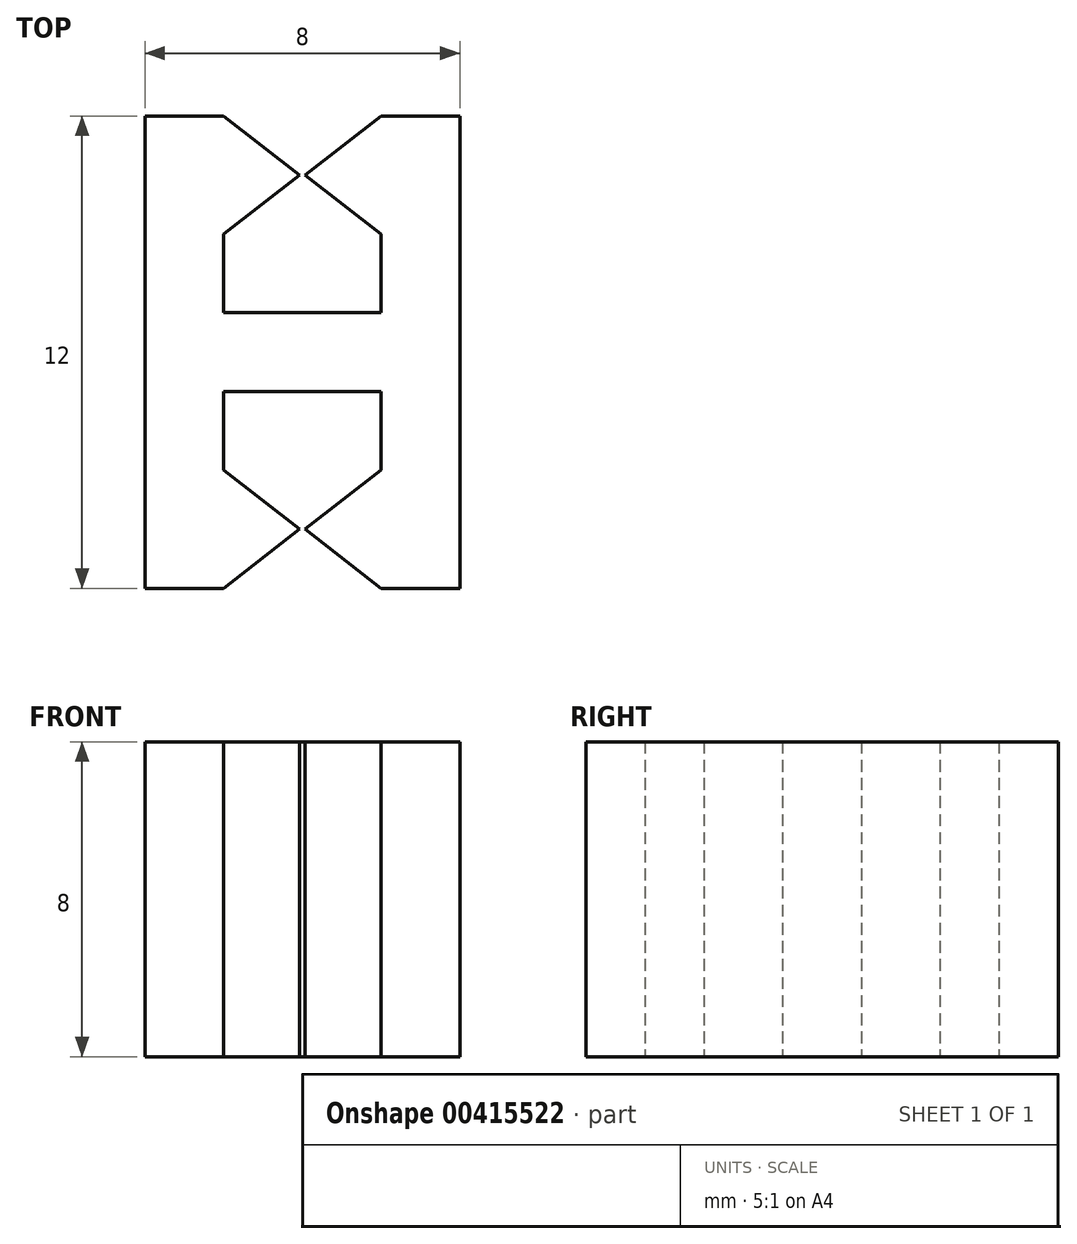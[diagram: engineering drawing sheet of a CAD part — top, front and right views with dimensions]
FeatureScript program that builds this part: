
annotation { "Feature Type Name" : "Feature", "Feature Type Description" : "" }
export const myFeature = defineFeature(function(context is Context, id is Id, definition is map)
    precondition{}
    {
        {
            var Q0;
            Q0=qCreatedBy(makeId("Top.planeOp"),FACE);
            var sketch = newSketch(context, id + "F0", { "sketchPlane" : qUnion([Q0])});
            skLineSegment(sketch, "E0", {"start": v(0, -1.2) * mm, "end": v(-2, -1.2) * mm});
            skLineSegment(sketch, "E1", {"start": v(-2, -1.2) * mm, "end": v(-2, -2.62) * mm});
            skLineSegment(sketch, "E2", {"start": v(-1.95, -2.76) * mm, "end": v(-1.4, -3.38) * mm});
            skLineSegment(sketch, "E3", {"start": v(-1.35, -3.45) * mm, "end": v(-1.35, -6) * mm, "construction": true});
            skLineSegment(sketch, "E4", {"start": v(-1.35, -6) * mm, "end": v(-4, -6) * mm});
            skLineSegment(sketch, "E5", {"start": v(-4, -6) * mm, "end": v(-4, 0) * mm});
            skArc(sketch, "E6", {"start": v(-1.35, -6) * mm, "mid": v(-0.07, -4.77) * mm, "end": v(-1.26, -3.45) * mm});
            skPoint(sketch, "E7.visualSharp", {"position": v(-2, -2.7) * mm});
            skArc(sketch, "E7.filletArc", {"start": v(-2, -2.62) * mm, "mid": v(-1.99, -2.7) * mm, "end": v(-1.95, -2.76) * mm});
            skPoint(sketch, "E8.visualSharp", {"position": v(-1.35, -3.45) * mm});
            skArc(sketch, "E8.filletArc", {"start": v(-1.4, -3.38) * mm, "mid": v(-1.34, -3.43) * mm, "end": v(-1.26, -3.45) * mm});
            skLineSegment(sketch, "E9", {"start": v(0, 0) * mm, "end": v(0, -3.87) * mm, "construction": true});
            skLineSegment(sketch, "E10", {"start": v(0, 0) * mm, "end": v(-4.58, 0) * mm, "construction": true});
            skArc(sketch, "E11.MirrorCS", {"start": v(1.4, -3.38) * mm, "mid": v(1.34, -3.43) * mm, "end": v(1.26, -3.45) * mm});
            skArc(sketch, "E12.MirrorCS", {"start": v(2, -2.62) * mm, "mid": v(1.99, -2.7) * mm, "end": v(1.95, -2.76) * mm});
            skPoint(sketch, "E13.MirrorP", {"position": v(1.35, -3.45) * mm});
            skPoint(sketch, "E14.MirrorP", {"position": v(2, -2.7) * mm});
            skArc(sketch, "E15.MirrorCS", {"start": v(1.35, -6) * mm, "mid": v(0.07, -4.77) * mm, "end": v(1.26, -3.45) * mm});
            skLineSegment(sketch, "E16.MirrorCS", {"start": v(0, -1.2) * mm, "end": v(2, -1.2) * mm});
            skLineSegment(sketch, "E17.MirrorCS", {"start": v(2, -1.2) * mm, "end": v(2, -2.62) * mm});
            skLineSegment(sketch, "E18.MirrorCS", {"start": v(1.35, -3.45) * mm, "end": v(1.35, -6) * mm, "construction": true});
            skLineSegment(sketch, "E19.MirrorCS", {"start": v(1.95, -2.76) * mm, "end": v(1.4, -3.38) * mm});
            skLineSegment(sketch, "E20.MirrorCS", {"start": v(1.35, -6) * mm, "end": v(4, -6) * mm});
            skLineSegment(sketch, "E21.MirrorCS", {"start": v(4, -6) * mm, "end": v(4, 0) * mm});
            skArc(sketch, "E22.MirrorCS", {"start": v(-1.4, 3.38) * mm, "mid": v(-1.34, 3.43) * mm, "end": v(-1.26, 3.45) * mm});
            skArc(sketch, "E23.MirrorCS", {"start": v(1.4, 3.38) * mm, "mid": v(1.34, 3.43) * mm, "end": v(1.26, 3.45) * mm});
            skLineSegment(sketch, "E24.MirrorCS", {"start": v(0, 1.2) * mm, "end": v(-2, 1.2) * mm});
            skLineSegment(sketch, "E25.MirrorCS", {"start": v(2, 1.2) * mm, "end": v(2, 2.62) * mm});
            skPoint(sketch, "E26.MirrorP", {"position": v(1.35, 3.45) * mm});
            skLineSegment(sketch, "E27.MirrorCS", {"start": v(0, 1.2) * mm, "end": v(2, 1.2) * mm});
            skArc(sketch, "E28.MirrorCS", {"start": v(2, 2.62) * mm, "mid": v(1.99, 2.7) * mm, "end": v(1.95, 2.76) * mm});
            skLineSegment(sketch, "E29.MirrorCS", {"start": v(-2, 1.2) * mm, "end": v(-2, 2.62) * mm});
            skArc(sketch, "E30.MirrorCS", {"start": v(1.35, 6) * mm, "mid": v(0.07, 4.77) * mm, "end": v(1.26, 3.45) * mm});
            skLineSegment(sketch, "E31.MirrorCS", {"start": v(-1.95, 2.76) * mm, "end": v(-1.4, 3.38) * mm});
            skLineSegment(sketch, "E32.MirrorCS", {"start": v(-1.35, 3.45) * mm, "end": v(-1.35, 6) * mm, "construction": true});
            skLineSegment(sketch, "E33.MirrorCS", {"start": v(-1.35, 6) * mm, "end": v(-4, 6) * mm});
            skLineSegment(sketch, "E34.MirrorCS", {"start": v(-4, 6) * mm, "end": v(-4, 0) * mm});
            skArc(sketch, "E35.MirrorCS", {"start": v(-2, 2.62) * mm, "mid": v(-1.99, 2.7) * mm, "end": v(-1.95, 2.76) * mm});
            skArc(sketch, "E36.MirrorCS", {"start": v(-1.35, 6) * mm, "mid": v(-0.07, 4.77) * mm, "end": v(-1.26, 3.45) * mm});
            skPoint(sketch, "E37.MirrorP", {"position": v(2, 2.7) * mm});
            skLineSegment(sketch, "E38.MirrorCS", {"start": v(1.95, 2.76) * mm, "end": v(1.4, 3.38) * mm});
            skPoint(sketch, "E39.MirrorP", {"position": v(-2, 2.7) * mm});
            skLineSegment(sketch, "E40.MirrorCS", {"start": v(1.35, 6) * mm, "end": v(4, 6) * mm});
            skLineSegment(sketch, "E41.MirrorCS", {"start": v(4, 6) * mm, "end": v(4, 0) * mm});
            skLineSegment(sketch, "E42.MirrorCS", {"start": v(1.35, 3.45) * mm, "end": v(1.35, 6) * mm, "construction": true});
            skPoint(sketch, "E43.MirrorP", {"position": v(-1.35, 3.45) * mm});
            skLineSegment(sketch, "E44", {"start": v(-1.35, -4.73) * mm, "end": v(-0.07, -4.73) * mm, "construction": true});
            skSolve(sketch);
        }
        {
            var Q0;
            Q0=qCreatedBy(makeId("Top.planeOp"),FACE);
            var sketch = newSketch(context, id + "F1", { "sketchPlane" : qUnion([Q0])});
            skLineSegment(sketch, "E45", {"start": v(-2, -3) * mm, "end": v(-0.07, -4.5) * mm});
            skLineSegment(sketch, "E46", {"start": v(-0.07, -4.5) * mm, "end": v(-2, -6) * mm});
            skLineSegment(sketch, "E47", {"start": v(-2, -6) * mm, "end": v(-4, -6) * mm});
            skLineSegment(sketch, "E48", {"start": v(-4, -6) * mm, "end": v(-4, 0) * mm});
            skLineSegment(sketch, "E49", {"start": v(-2, -6) * mm, "end": v(-2, -3) * mm, "construction": true});
            skLineSegment(sketch, "E50", {"start": v(-2, -4.5) * mm, "end": v(-0.07, -4.5) * mm, "construction": true});
            skLineSegment(sketch, "E51", {"start": v(-2, -3) * mm, "end": v(-2, -1) * mm});
            skLineSegment(sketch, "E52", {"start": v(-2, -1) * mm, "end": v(0, -1) * mm});
            skLineSegment(sketch, "E53", {"start": v(0, -1) * mm, "end": v(0, 0) * mm});
            skLineSegment(sketch, "E54", {"start": v(0, 0) * mm, "end": v(-4, 0) * mm});
            skSolve(sketch);
        }
        {
            var Q0;
            Q0 = qSketchRegion(id + "F1", true);
            extrude(context, id + "F2", {"entities" : qUnion([Q0]), "depth" : 8 * mm});
        }
        {
            var Q0;
            Q0=makeQuery(id+"F2.opExtrude","SWEPT_BODY",BODY,{"disambiguationData":[OSD([sQuery(id+"F1.wireOp",EDGE,"85Z40tRQ-Q0FO-HUkS-G0IK-aiCjI26RT9MV"),sQuery(id+"F1.wireOp",EDGE,"E45"),sQuery(id+"F1.wireOp",EDGE,"E46"),sQuery(id+"F1.wireOp",EDGE,"E47"),sQuery(id+"F1.wireOp",EDGE,"E48"),sQuery(id+"F1.wireOp",EDGE,"fy0ZgNiV-hdBj-VTZI-1ZR5-onnCdVL94iFC")])]});
            var Q1;
            Q1=qCreatedBy(makeId("Right.planeOp"),FACE);
            mirror(context, id + "F3", {"operationType" : NewBodyOperationType.ADD, "entities" : qUnion([Q0]), "mirrorPlane" : qUnion([Q1])});
        }
        {
            var Q0;
            Q0=makeQuery(id+"F2.opExtrude","SWEPT_BODY",BODY,{"disambiguationData":[OSD([sQuery(id+"F1.wireOp",EDGE,"E45"),sQuery(id+"F1.wireOp",EDGE,"E46"),sQuery(id+"F1.wireOp",EDGE,"E47"),sQuery(id+"F1.wireOp",EDGE,"E48"),sQuery(id+"F1.wireOp",EDGE,"E51"),sQuery(id+"F1.wireOp",EDGE,"E52"),sQuery(id+"F1.wireOp",EDGE,"E53"),sQuery(id+"F1.wireOp",EDGE,"E54")])]});
            var Q1;
            Q1=qCreatedBy(makeId("Front.planeOp"),FACE);
            mirror(context, id + "F4", {"operationType" : NewBodyOperationType.ADD, "entities" : qUnion([Q0]), "mirrorPlane" : qUnion([Q1])});
        }
    });
